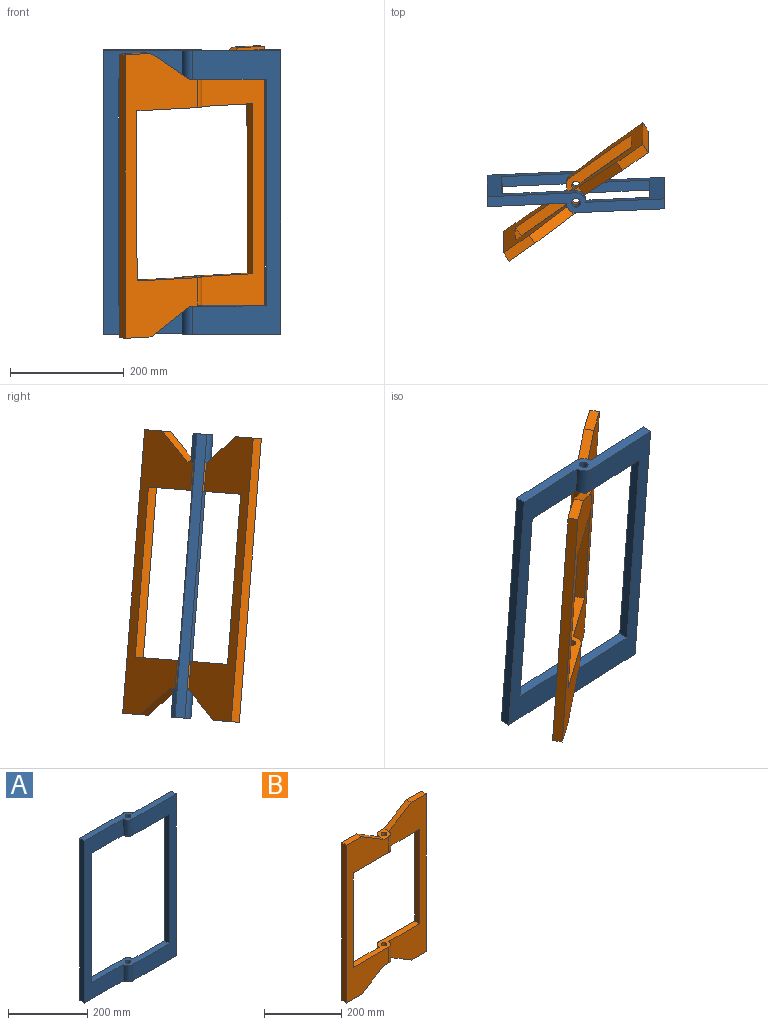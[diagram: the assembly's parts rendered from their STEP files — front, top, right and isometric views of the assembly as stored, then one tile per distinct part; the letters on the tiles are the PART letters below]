
ASSEMBLY  parts=2 mates=1
PART A: 18 faces, bbox 310x35x500 mm
  f0: cylinder r=17.5mm len=50mm, axis (0,0,-1), area 1374.4mm2, adj f6,f8,f13,f15
  f1: plane 500x137.5mm, normal (0,-1,0), area 23750mm2, adj f2,f3,f9,f12,f13,f15,f16,f17
  f2: cylinder r=17.5mm len=50mm, axis (0,0,-1), area 1374.4mm2, adj f1,f10,f13,f15
  f3: cylinder r=17.5mm len=50mm, axis (0,0,-1), area 1374.4mm2, adj f1,f10,f12,f16
  f4: cylinder r=7.5mm len=50mm, axis (0,0,-1), area 2356.2mm2, adj f13,f15
  f5: cylinder r=7.5mm len=50mm, axis (0,0,-1), area 2356.2mm2, adj f12,f16
  f6: plane 500x137.5mm, normal (0,1,0), area 23750mm2, adj f0,f7,f11,f12,f13,f14,f15,f16
  f7: cylinder r=17.5mm len=50mm, axis (0,0,-1), area 1374.4mm2, adj f6,f8,f12,f16
  f8: plane 500x155mm, normal (0,1,0), area 25500mm2, adj f0,f7,f9,f12,f13,f15,f16,f17
  f9: plane 500x17.5mm, normal (-1,0,0), area 8750mm2, adj f1,f8,f12,f13
  f10: plane 500x155mm, normal (0,-1,0), area 25500mm2, adj f2,f3,f11,f12,f13,f14,f15,f16
  f11: plane 500x17.5mm, normal (1,0,0), area 8750mm2, adj f6,f10,f12,f13
  f12: plane 310x35mm, normal (0,0,1), area 5729.3mm2, adj f1,f3,f5,f6,f7,f8,f9,f10
  f13: plane 310x35mm, normal (0,0,-1), area 5729.3mm2, adj f0,f1,f2,f4,f6,f8,f9,f10
  f14: plane 400x17.5mm, normal (-1,0,0), area 7000mm2, adj f6,f10,f15,f16
  f15: plane 260x35mm, normal (0,0,1), area 4854.3mm2, adj f0,f1,f2,f4,f6,f8,f10,f14
  f16: plane 260x35mm, normal (0,0,-1), area 4854.3mm2, adj f1,f3,f5,f6,f7,f8,f10,f14
  f17: plane 400x17.5mm, normal (1,0,0), area 7000mm2, adj f1,f8,f15,f16
PART B: 26 faces, bbox 310x35x500 mm
  f0: plane 500x155mm, normal (0,-1,0), area 32626.1mm2, adj f4,f8,f11,f13,f14,f15,f16,f18
  f1: plane 500x155mm, normal (0,1,0), area 32626.1mm2, adj f2,f7,f9,f10,f12,f15,f17,f18
  f2: cylinder r=17.5mm len=50.01mm, axis (0,0,-1), area 1374.4mm2, adj f1,f3,f18,f19,f24
  f3: plane 500x137.5mm, normal (0,1,0), area 30876.1mm2, adj f2,f7,f11,f13,f14,f16,f19,f22
  f4: cylinder r=17.5mm len=50.01mm, axis (0,0,-1), area 1374.4mm2, adj f0,f5,f18,f20,f24
  f5: plane 500x137.5mm, normal (0,-1,0), area 30876.1mm2, adj f4,f8,f9,f10,f12,f17,f20,f23
  f6: cylinder r=7.5mm len=50mm, axis (0,0,-1), area 2356.2mm2, adj f18,f24
  f7: cylinder r=17.5mm len=50.01mm, axis (0,0,-1), area 1374.4mm2, adj f1,f3,f15,f16,f25
  f8: cylinder r=17.5mm len=50.01mm, axis (0,0,-1), area 1374.4mm2, adj f0,f5,f15,f17,f25
  f9: plane 55.01x17.5mm, normal (0,0,1), area 962.7mm2, adj f1,f5,f12,f17
  f10: plane 55.01x17.5mm, normal (0,0,-1), area 962.7mm2, adj f1,f5,f12,f20
  f11: plane 500x17.5mm, normal (-1,0,0), area 8750mm2, adj f0,f3,f13,f14
  f12: plane 500x17.5mm, normal (1,0,0), area 8750mm2, adj f1,f5,f9,f10
  f13: plane 55.01x17.5mm, normal (0,0,1), area 962.7mm2, adj f0,f3,f11,f16
  f14: plane 55.01x17.5mm, normal (0,0,-1), area 962.7mm2, adj f0,f3,f11,f19
  f15: plane 35x34.98mm, normal (0,0,1), area 916.5mm2, adj f0,f1,f7,f8,f16,f17,f21
  f16: plane 82.5x50mm, normal (0.52,0,0.86), area 1688.2mm2, adj f0,f3,f7,f13,f15
  f17: plane 82.5x50mm, normal (-0.52,0,0.86), area 1688.2mm2, adj f1,f5,f8,f9,f15
  f18: plane 35x34.98mm, normal (0,0,-1), area 916.5mm2, adj f0,f1,f2,f4,f6,f19,f20
  f19: plane 82.5x50mm, normal (0.52,0,-0.86), area 1688.2mm2, adj f0,f2,f3,f14,f18
  f20: plane 82.5x50mm, normal (-0.52,0,-0.86), area 1688.2mm2, adj f1,f4,f5,f10,f18
  f21: cylinder r=7.5mm len=50mm, axis (0,0,-1), area 2356.2mm2, adj f15,f25
  f22: plane 300x17.5mm, normal (1,0,0), area 5250mm2, adj f0,f3,f24,f25
  f23: plane 300x17.5mm, normal (-1,0,0), area 5250mm2, adj f1,f5,f24,f25
  f24: plane 260x35mm, normal (0,0,1), area 4854.3mm2, adj f0,f1,f2,f3,f4,f5,f6,f22
  f25: plane 260x35mm, normal (0,0,-1), area 4854.3mm2, adj f0,f1,f3,f5,f7,f8,f21,f22
PLACE A rot(axis=(0.87,-0.02,0.5),5.1deg) t=(55.79,63.64,29.98)mm
PLACE B rot(axis=(0.12,-0.04,0.99),35.1deg) t=(55.84,63.55,29.97)mm
MATE revolute A.f0 <-> B.f2  axis (0,-0.08,1) through (55.78,59.77,79.83)mm
